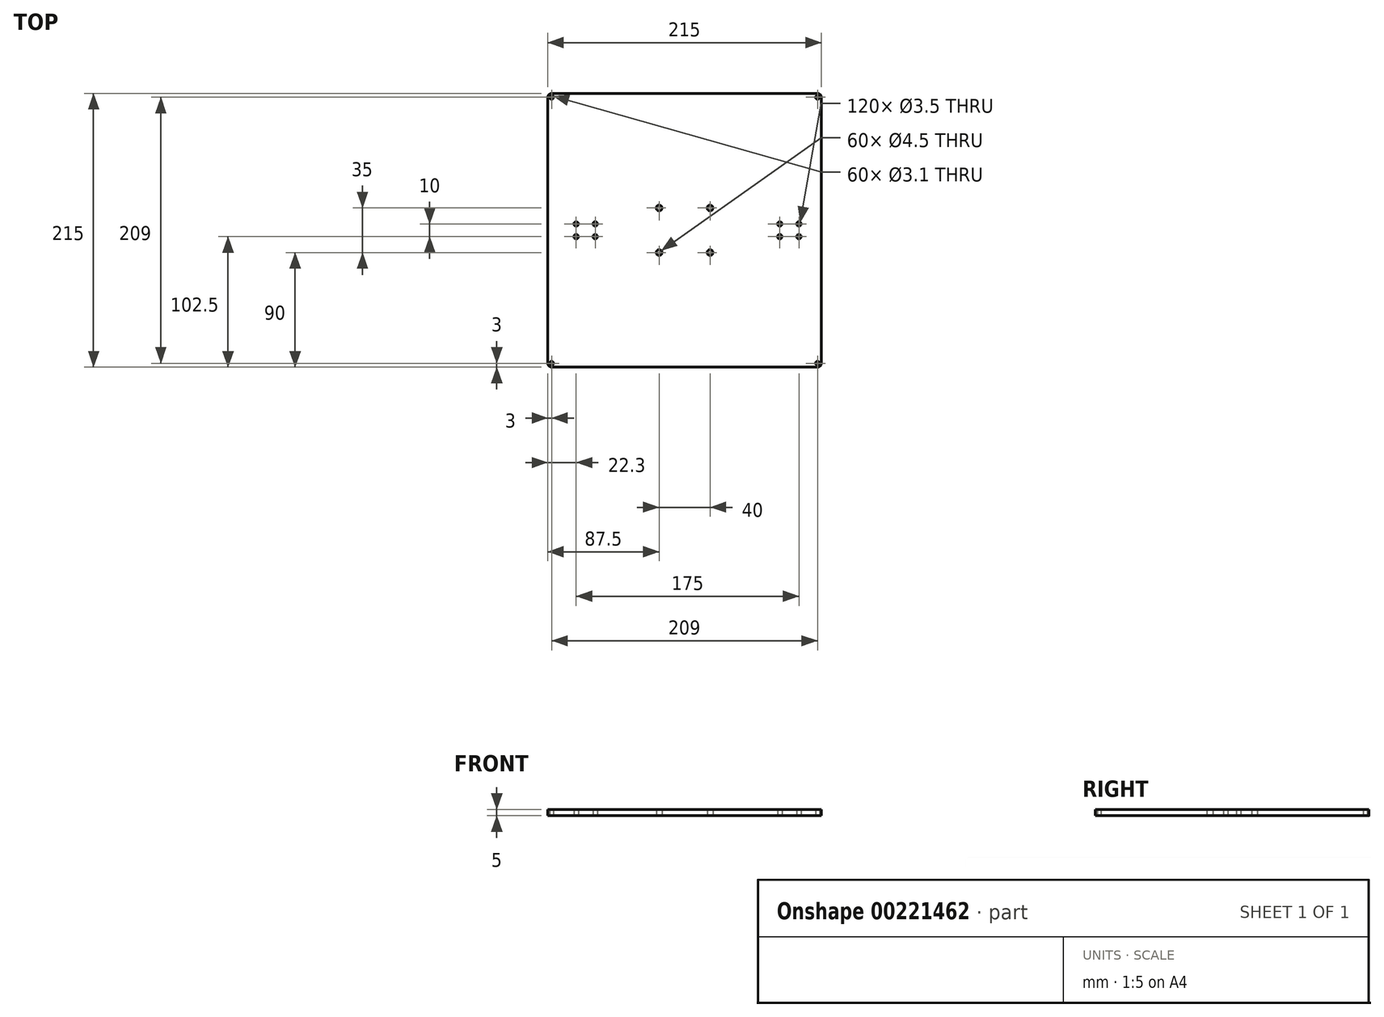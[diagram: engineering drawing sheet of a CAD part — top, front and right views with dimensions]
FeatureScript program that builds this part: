
annotation { "Feature Type Name" : "Feature", "Feature Type Description" : "" }
export const myFeature = defineFeature(function(context is Context, id is Id, definition is map)
    precondition{}
    {
        {
            var Q0;
            Q0=qCreatedBy(makeId("Top.planeOp"),FACE);
            var sketch = newSketch(context, id + "F0", { "sketchPlane" : qUnion([Q0])});
            skLineSegment(sketch, "E0.bottom", {"start": v(3, 0) * mm, "end": v(212, 0) * mm});
            skLineSegment(sketch, "E0.top", {"start": v(3, 215) * mm, "end": v(212, 215) * mm});
            skLineSegment(sketch, "E0.left", {"start": v(0, 3) * mm, "end": v(0, 212) * mm});
            skLineSegment(sketch, "E0.right", {"start": v(215, 3) * mm, "end": v(215, 212) * mm});
            skLineSegment(sketch, "E1.bottom", {"start": v(7.5, 214) * mm, "end": v(207.5, 214) * mm, "construction": true});
            skLineSegment(sketch, "E1.top", {"start": v(7.5, 1) * mm, "end": v(207.5, 1) * mm, "construction": true});
            skLineSegment(sketch, "E1.left", {"start": v(7.5, 214) * mm, "end": v(7.5, 1) * mm, "construction": true});
            skLineSegment(sketch, "E1.right", {"start": v(207.5, 214) * mm, "end": v(207.5, 1) * mm, "construction": true});
            skPoint(sketch, "E2", {"position": v(7.5, 107.5) * mm});
            skLineSegment(sketch, "E3", {"start": v(0, 107.5) * mm, "end": v(215, 107.5) * mm, "construction": true});
            skLineSegment(sketch, "E4.bottom", {"start": v(182.3, 112.5) * mm, "end": v(197.3, 112.5) * mm, "construction": true});
            skLineSegment(sketch, "E4.top", {"start": v(182.3, 102.5) * mm, "end": v(197.3, 102.5) * mm, "construction": true});
            skLineSegment(sketch, "E4.left", {"start": v(182.3, 112.5) * mm, "end": v(182.3, 102.5) * mm, "construction": true});
            skLineSegment(sketch, "E4.right", {"start": v(197.3, 112.5) * mm, "end": v(197.3, 102.5) * mm, "construction": true});
            skLineSegment(sketch, "E5.bottom", {"start": v(22.3, 112.5) * mm, "end": v(37.3, 112.5) * mm, "construction": true});
            skLineSegment(sketch, "E5.top", {"start": v(22.3, 102.5) * mm, "end": v(37.3, 102.5) * mm, "construction": true});
            skLineSegment(sketch, "E5.left", {"start": v(22.3, 112.5) * mm, "end": v(22.3, 102.5) * mm, "construction": true});
            skLineSegment(sketch, "E5.right", {"start": v(37.3, 112.5) * mm, "end": v(37.3, 102.5) * mm, "construction": true});
            skPoint(sketch, "E6", {"position": v(182.3, 107.5) * mm});
            skCircle(sketch, "E7", {"center": v(22.3, 112.5) * mm, "radius": 1.75 * mm});
            skCircle(sketch, "E8", {"center": v(37.3, 112.5) * mm, "radius": 1.75 * mm});
            skCircle(sketch, "E9", {"center": v(182.3, 112.5) * mm, "radius": 1.75 * mm});
            skCircle(sketch, "E10", {"center": v(197.3, 112.5) * mm, "radius": 1.75 * mm});
            skCircle(sketch, "E11.MirrorC", {"center": v(22.3, 102.5) * mm, "radius": 1.75 * mm});
            skCircle(sketch, "E12.MirrorC", {"center": v(37.3, 102.5) * mm, "radius": 1.75 * mm});
            skCircle(sketch, "E13.MirrorC", {"center": v(182.3, 102.5) * mm, "radius": 1.75 * mm});
            skCircle(sketch, "E14.MirrorC", {"center": v(197.3, 102.5) * mm, "radius": 1.75 * mm});
            skLineSegment(sketch, "E15.top", {"start": v(87.5, 90) * mm, "end": v(127.5, 90) * mm, "construction": true});
            skLineSegment(sketch, "E15.left", {"start": v(87.5, 125) * mm, "end": v(87.5, 90) * mm, "construction": true});
            skLineSegment(sketch, "E15.right", {"start": v(127.5, 125) * mm, "end": v(127.5, 90) * mm, "construction": true});
            skCircle(sketch, "E16", {"center": v(127.5, 90) * mm, "radius": 2.25 * mm});
            skCircle(sketch, "E17", {"center": v(87.5, 90) * mm, "radius": 2.25 * mm});
            skCircle(sketch, "E18.MirrorC", {"center": v(87.5, 125) * mm, "radius": 2.25 * mm});
            skCircle(sketch, "E19.MirrorC", {"center": v(127.5, 125) * mm, "radius": 2.25 * mm});
            skCircle(sketch, "E20", {"center": v(3, 3) * mm, "radius": 1.55 * mm});
            skCircle(sketch, "E21", {"center": v(212, 3) * mm, "radius": 1.55 * mm});
            skCircle(sketch, "E22.MirrorC", {"center": v(3, 212) * mm, "radius": 1.55 * mm});
            skCircle(sketch, "E23.MirrorC", {"center": v(212, 212) * mm, "radius": 1.55 * mm});
            skLineSegment(sketch, "E24", {"start": v(3, 3) * mm, "end": v(212, 3) * mm, "construction": true});
            skPoint(sketch, "E25", {"position": v(107.5, 3) * mm});
            skPoint(sketch, "E26", {"position": v(107.5, 0) * mm});
            skLineSegment(sketch, "E27", {"start": v(3, 3) * mm, "end": v(3, 212) * mm, "construction": true});
            skPoint(sketch, "E28", {"position": v(3, 107.5) * mm});
            skPoint(sketch, "E29.visualSharp", {"position": v(0, 215) * mm});
            skArc(sketch, "E29.filletArc", {"start": v(3, 215) * mm, "mid": v(0.88, 214.12) * mm, "end": v(0, 212) * mm});
            skPoint(sketch, "E30.visualSharp", {"position": v(215, 215) * mm});
            skArc(sketch, "E30.filletArc", {"start": v(215, 212) * mm, "mid": v(214.12, 214.12) * mm, "end": v(212, 215) * mm});
            skPoint(sketch, "E31.visualSharp", {"position": v(215, 0) * mm});
            skArc(sketch, "E31.filletArc", {"start": v(212, 0) * mm, "mid": v(214.12, 0.88) * mm, "end": v(215, 3) * mm});
            skPoint(sketch, "E32.visualSharp", {"position": v(0, 0) * mm});
            skArc(sketch, "E32.filletArc", {"start": v(0, 3) * mm, "mid": v(0.88, 0.88) * mm, "end": v(3, 0) * mm});
            skSolve(sketch);
        }
        {
            var Q0;
            Q0=makeQuery(id+"F0.imprint","IMPRINT",FACE,{"disambiguationData":[TD([[makeQuery(id+"F0.imprint","IMPRINT",EDGE,{"derivedFrom":sQuery(id+"F0.wireOp",EDGE,"E0.bottom")}),1.0]])]});
            extrude(context, id + "F1", {"entities" : qUnion([Q0]), "depth" : 5 * mm});
        }
    });
